# Revit family: axor_complete_set_with_flexaplus_finish_set_58315000
name_source: partatom
category: Plumbing Fixtures
revit_build: Autodesk Revit 2015 (Build: 20140903_1530(x64)
units: mm (PartAtom-declared; Revit-internal decimal feet)

## types (1)
- Chrome 000
    BIMobject category = Drainage
    BOSUseNativeGeometries = 1
    Default Elevation = 1219 mm
    Design country = Germany
    EAN code = https://4059625077672
    Edition number = 1
    IFC Classification = Sanitary Terminal
    Installation instructions = https://pro.hansgrohe-int.com
    Manufacturer country = Germany
    Manufacturer name = AXOR
    Masterformat 2014 Code = 33 37 00
    Masterformat 2014 Description = Overflow Control
    Material main = Chrome
    NBS Reference Code = 35-06-07
    NBS Reference Description = Bath Water Supply Fittings
    Nominal height = 0
    Nominal width = 0
    OmniClass Code = 23-31 00 00
    OmniClass Description = Plumbing Specific Products and Equipment
    Product Guid = 367116ec-9821-40c2-b213-1d9c51a8b023
    Product SKU = 58315000
    Product data url = https://bimobject.com
    Product family = Wastes and overflows
    Product group = Bath filler with wastes and overflow for bath tubs
    Product name = AXOR Complete set with Flexaplus finish set 58315000
    Product url = https://pro.hansgrohe-int.com
    QR code = http://bimobject.com
    Technical description = https://pro.hansgrohe-int.com
    UNSPSC Code = 3018
    Uniclass 1.4 Code = L721
    Uniclass 1.4 Description = Sanitary equipment
    Uniclass 2.0 Code = PR-35-06-07
    Uniclass 2.0 Description = Bath Water Supply Fittings
    Uniclass 2015 Code = Pr_70_55_96
    Uniclass 2015 Name = Waste water outlets and plugs
    Uniformat II Code = D2090
    Uniformat II Description = Other Plumbing Systems
    Weight Net (Kg) = 0

## geometry (parser evidence)
native form markers: Sweep x1
no freeform markers — native parametric forms only
